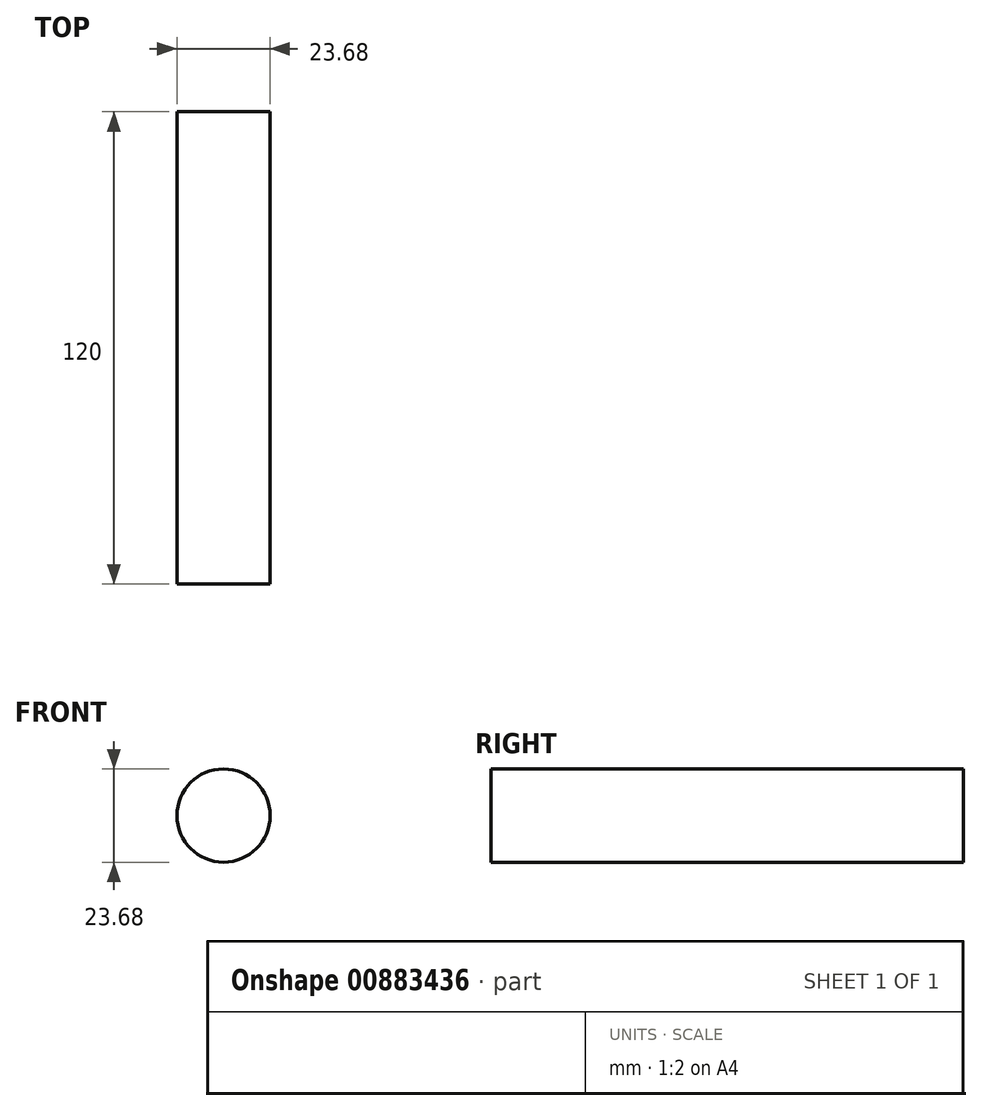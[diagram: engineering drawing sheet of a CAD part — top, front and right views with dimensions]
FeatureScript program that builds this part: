
annotation { "Feature Type Name" : "Feature", "Feature Type Description" : "" }
export const myFeature = defineFeature(function(context is Context, id is Id, definition is map)
    precondition{}
    {
        {
            var Q0;
            Q0=qCreatedBy(makeId("Front.planeOp"),FACE);
            var sketch = newSketch(context, id + "F0", { "sketchPlane" : qUnion([Q0])});
            skCircle(sketch, "E0", {"center": v(0, 0) * mm, "radius": 11.84 * mm});
            skSolve(sketch);
        }
        {
            var Q0;
            Q0 = qSketchRegion(id + "F0", true);
            extrude(context, id + "F1", {"entities" : qUnion([Q0]), "depth" : 120 * mm, "offsetDistance" : 25.4 * mm});
        }
    });
